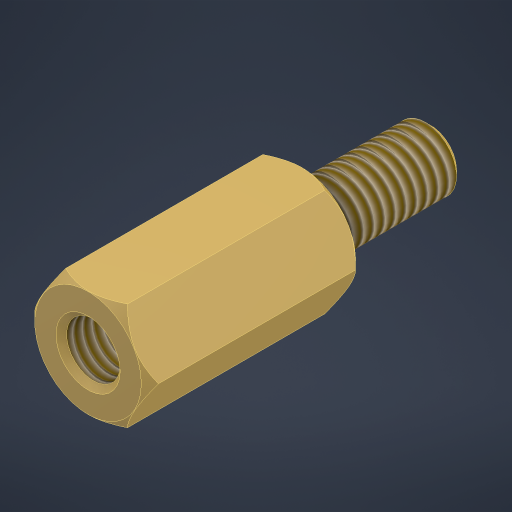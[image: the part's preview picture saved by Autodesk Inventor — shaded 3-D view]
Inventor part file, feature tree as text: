
AUTODESK INVENTOR PART (.ipt)
format: ipt  version: 2023 (Build 270158000, 158)  size: 249,856 bytes
history: native  units: in
note: dims shown in document units (in); Inventor stores cm internally (conversion verified against a paired STEP export)
features: thread x2, other x1
ambient origin geometry x8: Origin, YZ Plane, XZ Plane, XY Plane, X Axis, Y Axis, Z Axis, Center Point
bodies: Solid1 (feature_tree)
feature tree (3):
  thread  "Thread1"  [1 undecoded]
  thread  "Thread2"  [1 undecoded]
  other  "InnerChamfer"
note: 2 required parameter values undecoded (feature->parameter linkage not recoverable at this tier; creation-order binding heuristic only, values carry confidence <= 0.55)
